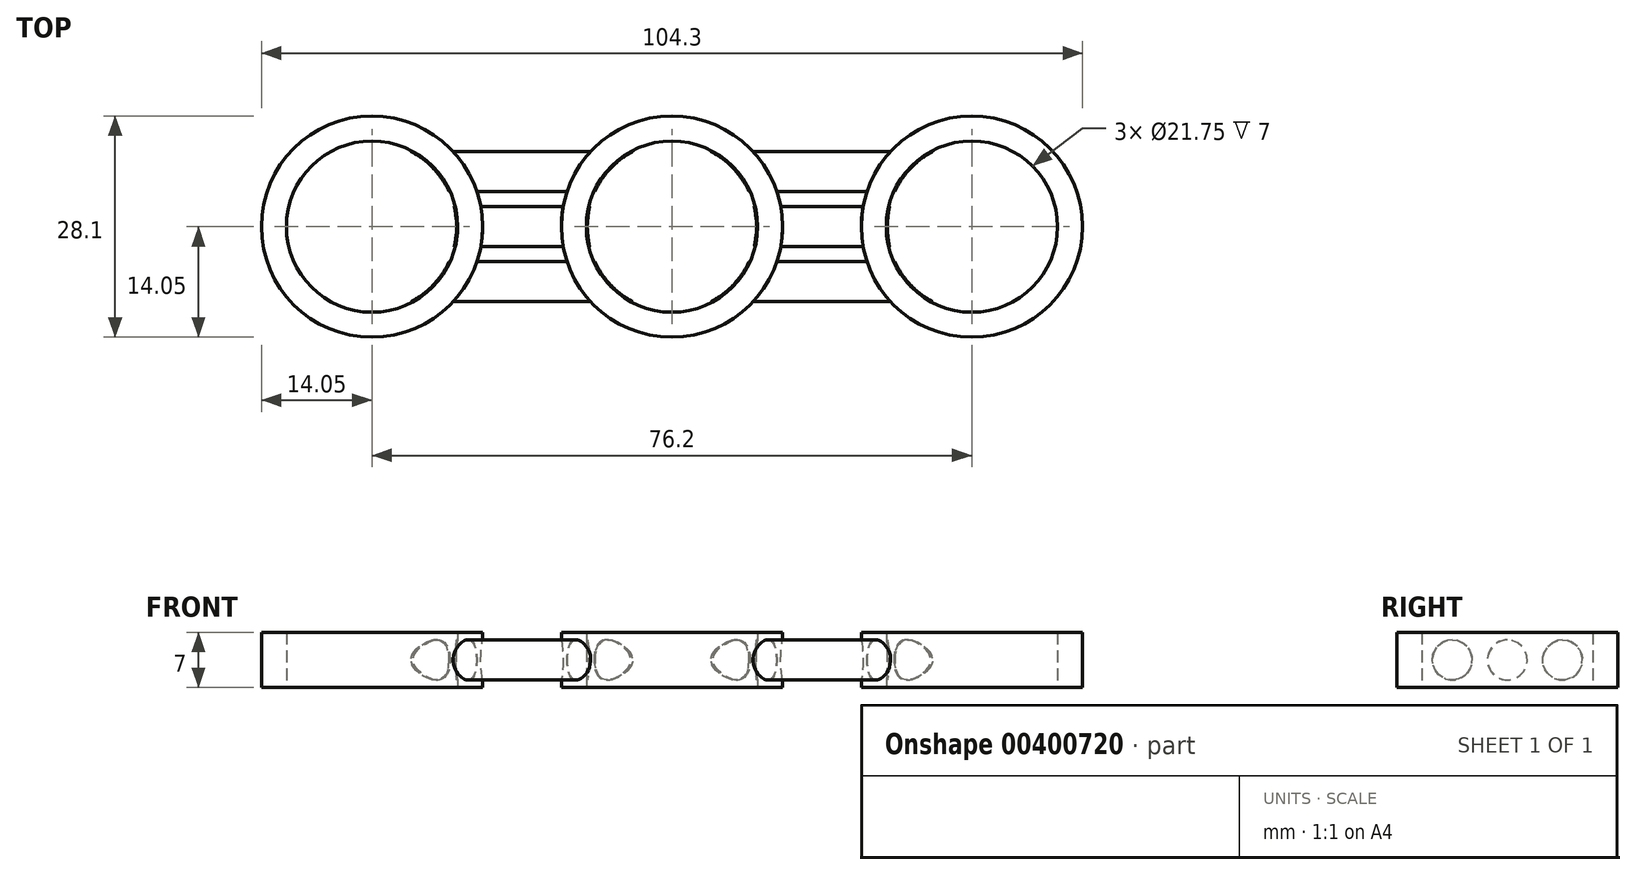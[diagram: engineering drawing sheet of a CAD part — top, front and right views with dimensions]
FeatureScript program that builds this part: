
annotation { "Feature Type Name" : "Feature", "Feature Type Description" : "" }
export const myFeature = defineFeature(function(context is Context, id is Id, definition is map)
    precondition{}
    {
        {
            var Q0;
            Q0=qCreatedBy(makeId("Top.planeOp"),FACE);
            var sketch = newSketch(context, id + "F0", { "sketchPlane" : qUnion([Q0])});
            skCircle(sketch, "E0", {"center": v(0, 0) * mm, "radius": 10.88 * mm});
            skCircle(sketch, "E1", {"center": v(-38.1, 0) * mm, "radius": 10.88 * mm});
            skCircle(sketch, "E2", {"center": v(38.1, 0) * mm, "radius": 10.88 * mm});
            skCircle(sketch, "E3", {"center": v(-38.1, 0) * mm, "radius": 14.05 * mm});
            skCircle(sketch, "E4", {"center": v(0, 0) * mm, "radius": 14.05 * mm});
            skCircle(sketch, "E5", {"center": v(38.1, 0) * mm, "radius": 14.05 * mm});
            skSolve(sketch);
        }
        {
            var Q0;
            Q0=makeQuery(id+"F0.imprint","IMPRINT",FACE,{"disambiguationData":[TD([[makeQuery(id+"F0.imprint","IMPRINT",EDGE,{"derivedFrom":sQuery(id+"F0.wireOp",EDGE,"E1")}),-1.0]])]});
            var Q1;
            Q1=makeQuery(id+"F0.imprint","IMPRINT",FACE,{"disambiguationData":[TD([[makeQuery(id+"F0.imprint","IMPRINT",EDGE,{"derivedFrom":sQuery(id+"F0.wireOp",EDGE,"E0")}),-1.0]])]});
            var Q2;
            Q2=makeQuery(id+"F0.imprint","IMPRINT",FACE,{"disambiguationData":[TD([[makeQuery(id+"F0.imprint","IMPRINT",EDGE,{"derivedFrom":sQuery(id+"F0.wireOp",EDGE,"E2")}),-1.0]])]});
            extrude(context, id + "F1", {"entities" : qUnion([Q0, Q1, Q2]), "depth" : 7 * mm});
        }
        {
            var Q0;
            Q0=qCreatedBy(makeId("Right.planeOp"),FACE);
            var sketch = newSketch(context, id + "F2", { "sketchPlane" : qUnion([Q0])});
            skCircle(sketch, "E6", {"center": v(0, 3.5) * mm, "radius": 2.54 * mm});
            skCircle(sketch, "E7", {"center": v(7, 3.5) * mm, "radius": 2.54 * mm});
            skCircle(sketch, "E8", {"center": v(-7, 3.5) * mm, "radius": 2.54 * mm});
            skSolve(sketch);
        }
        {
            var Q0;
            Q0=makeQuery(id+"F2.imprint","IMPRINT",FACE,{"disambiguationData":[TD([[makeQuery(id+"F2.imprint","IMPRINT",EDGE,{"derivedFrom":sQuery(id+"F2.wireOp",EDGE,"E8")}),1.0]])]});
            var Q1;
            Q1=makeQuery(id+"F2.imprint","IMPRINT",FACE,{"disambiguationData":[TD([[makeQuery(id+"F2.imprint","IMPRINT",EDGE,{"derivedFrom":sQuery(id+"F2.wireOp",EDGE,"E6")}),1.0]])]});
            var Q2;
            Q2=makeQuery(id+"F2.imprint","IMPRINT",FACE,{"disambiguationData":[TD([[makeQuery(id+"F2.imprint","IMPRINT",EDGE,{"derivedFrom":sQuery(id+"F2.wireOp",EDGE,"E7")}),1.0]])]});
            extrude(context, id + "F3", {"entities" : qUnion([Q0, Q1, Q2]), "operationType" : NewBodyOperationType.ADD, "endBound" : BoundingType.SYMMETRIC, "depth" : 76.2 * mm});
        }
        {
            var Q0;
            Q0=makeQuery(id+"F1.opExtrude","CAP_FACE",FACE,{"disambiguationData":[OSD([sQuery(id+"F0.wireOp",EDGE,"E2"),sQuery(id+"F0.wireOp",EDGE,"E5")])],"isStart":false});
            var sketch = newSketch(context, id + "F4", { "sketchPlane" : qUnion([Q0])});
            skCircle(sketch, "E9", {"center": v(0, 0) * mm, "radius": 10.75 * mm});
            skCircle(sketch, "E10", {"center": v(-38.1, 0) * mm, "radius": 10.75 * mm});
            skCircle(sketch, "E11", {"center": v(38.1, 0) * mm, "radius": 10.75 * mm});
            skSolve(sketch);
        }
        {
            var Q0;
            Q0=makeQuery(id+"F4.imprint","IMPRINT",FACE,{"disambiguationData":[TD([[makeQuery(id+"F4.imprint","IMPRINT",EDGE,{"derivedFrom":sQuery(id+"F4.wireOp",EDGE,"E10")}),1.0]])]});
            var Q1;
            Q1=makeQuery(id+"F4.imprint","IMPRINT",FACE,{"disambiguationData":[TD([[makeQuery(id+"F4.imprint","IMPRINT",EDGE,{"derivedFrom":sQuery(id+"F4.wireOp",EDGE,"E9")}),1.0]])]});
            var Q2;
            Q2=makeQuery(id+"F4.imprint","IMPRINT",FACE,{"disambiguationData":[TD([[makeQuery(id+"F4.imprint","IMPRINT",EDGE,{"derivedFrom":sQuery(id+"F4.wireOp",EDGE,"E11")}),1.0]])]});
            extrude(context, id + "F5", {"entities" : qUnion([Q0, Q1, Q2]), "operationType" : NewBodyOperationType.REMOVE, "oppositeDirection" : true, "depth" : 25.4 * mm});
        }
    });
